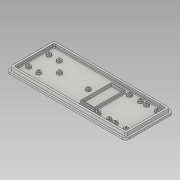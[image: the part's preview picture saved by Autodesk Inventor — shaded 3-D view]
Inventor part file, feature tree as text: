
AUTODESK INVENTOR PART (.ipt)
format: ipt  version: 2019 (Build 230136000, 136)  size: 612,864 bytes
history: native  units: mm
features: projected_geometry x17, sketch x5, extrude x4, fillet x4, other x1, hole x1
ambient origin geometry x8: Origin, YZ Plane, XZ Plane, XY Plane, X Axis, Y Axis, Z Axis, Center Point
bodies: Body1 (feature_tree)
feature tree (32):
  other  "Sólido1"
  extrude  "Extrusión1"  Depth=44.0mm
  extrude  "Extrusión2"  Depth=36.0mm
  fillet  "Empalme1"  Radius=18.0mm
  fillet  "Empalme2"  Radius=43.0mm
  extrude  "Extrusión3"  Depth=20.0mm
  extrude  "Extrusión4"  Depth=5.0mm
  fillet  "Empalme3"  Radius=5.0mm
  fillet  "Empalme4"  Radius=5.0mm
  hole  "Agujero1"  [1 undecoded]
  sketch  "Boceto1"  dims[d0=21.0mm d1=44.0mm]
  sketch  "Boceto2"  dims[d2=57.0mm d3=36.0mm d4=18.0mm d5=43.0mm]
  projected_geometry  "Contorno proyectado1"
  sketch  "Boceto4"  dims[d6=20.0mm d7=50.0mm]
  projected_geometry  "Contorno proyectado2"
  sketch  "Boceto5"  dims[d8=20.0mm d9=50.0mm d10=5.0mm d11=5.0mm]
  projected_geometry  "Contorno proyectado3"
  sketch  "Boceto6"  dims[d12=5.0mm d13=5.0mm d15=9.5mm d16=9.5mm d17=70.0mm d18=175.0mm d19=2.8mm d20=0.0mm d21=16.0mm d22=46.0mm d23=16.0mm d24=46.0mm d25=42.0mm d26=15.0mm d27=30.0mm d28=6.0mm d29=6.0mm d30=6.0mm d31=6.0mm d32=6.0mm d33=6.0mm d34=6.0mm d35=6.0mm d36=6.0mm d37=6.0mm d38=6.0mm d39=6.0mm d40=6.0mm d41=6.0mm d42=2.8mm d43=0.0mm d44=0.5mm d45=5.0mm d46=2.82mm d47=2.8mm d48=2.0mm d49=5.0mm d50=0.0mm d51=17.6mm d52=43.1mm d53=20.0mm d54=45.0mm d55=4.0mm d56=0.0mm d57=1.0mm d58=1.0mm d59=1.8mm d60=6.0mm d61=2.5mm d62=2.0mm d63=90.0deg d64=5.0mm d65=20.594885mm]
  projected_geometry  "Contorno proyectado4"
  projected_geometry  "Contorno proyectado5"
  projected_geometry  "Contorno proyectado6"
  projected_geometry  "Contorno proyectado7"
  projected_geometry  "Contorno proyectado8"
  projected_geometry  "Contorno proyectado9"
  projected_geometry  "Contorno proyectado10"
  projected_geometry  "Contorno proyectado11"
  projected_geometry  "Contorno proyectado12"
  projected_geometry  "Contorno proyectado13"
  projected_geometry  "Contorno proyectado14"
  projected_geometry  "Contorno proyectado15"
  projected_geometry  "Contorno proyectado16"
  projected_geometry  "Contorno proyectado17"
note: 1 required parameter value undecoded (feature->parameter linkage not recoverable at this tier; creation-order binding heuristic only, values carry confidence <= 0.55)
